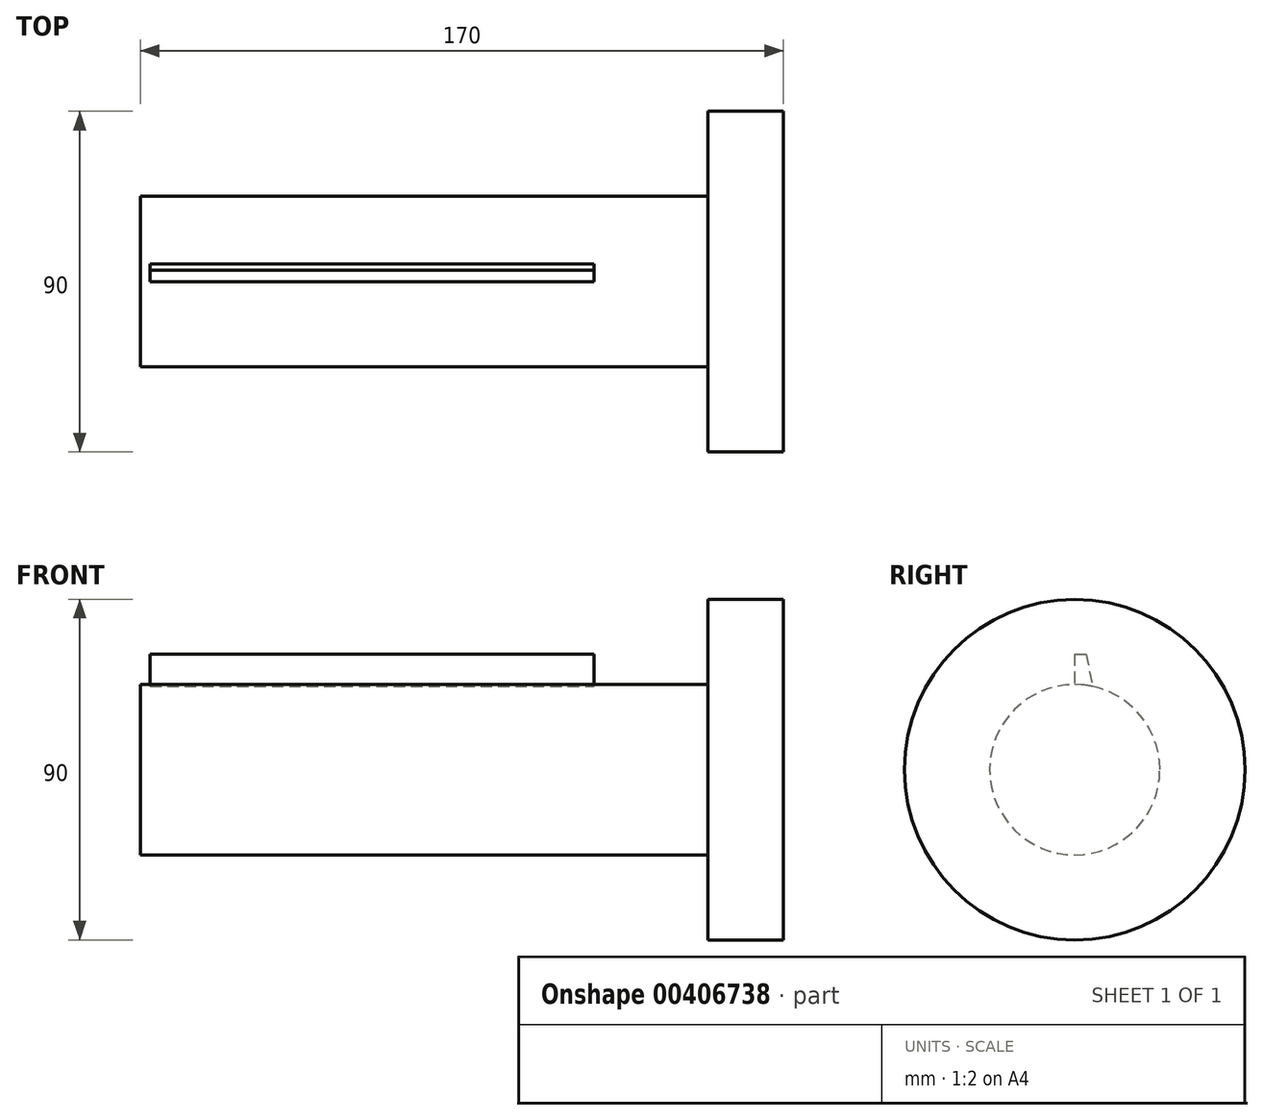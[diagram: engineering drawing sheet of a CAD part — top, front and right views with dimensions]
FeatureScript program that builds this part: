
annotation { "Feature Type Name" : "Feature", "Feature Type Description" : "" }
export const myFeature = defineFeature(function(context is Context, id is Id, definition is map)
    precondition{}
    {
        {
            var Q0;
            Q0=qCreatedBy(makeId("Front.planeOp"),FACE);
            var sketch = newSketch(context, id + "F0", { "sketchPlane" : qUnion([Q0])});
            skLineSegment(sketch, "E0", {"start": v(-150, 0) * mm, "end": v(20, 0) * mm});
            skLineSegment(sketch, "E1", {"start": v(20, 0) * mm, "end": v(20, 45) * mm});
            skLineSegment(sketch, "E2", {"start": v(20, 45) * mm, "end": v(0, 45) * mm});
            skLineSegment(sketch, "E3", {"start": v(0, 45) * mm, "end": v(0, 22.5) * mm});
            skLineSegment(sketch, "E4", {"start": v(0, 22.5) * mm, "end": v(-150, 22.5) * mm});
            skLineSegment(sketch, "E5", {"start": v(-150, 22.5) * mm, "end": v(-150, 0) * mm});
            skLineSegment(sketch, "E6", {"start": v(-127.35, 0) * mm, "end": v(126.66, 0) * mm, "construction": true});
            skSolve(sketch);
        }
        {
            var Q0;
            Q0 = qSketchRegion(id + "F0", true);
            var Q1;
            Q1=sQuery(id+"F0.wireOp",EDGE,"E6");
            revolve(context, id + "F1", {"entities" : qUnion([Q0]), "axis" : qUnion([Q1]), "revolveType" : RevolveType.FULL});
        }
        {
            var Q0;
            Q0=qCreatedBy(makeId("Right.planeOp"),FACE);
            cPlane(context, id + "F2", {"entities" : qUnion([Q0]), "cplaneType" : CPlaneType.OFFSET, "offset" : 30 * mm, "oppositeDirection" : true, "width" : 150 * mm, "height" : 150 * mm});
        }
        {
            var Q0;
            Q0=qCreatedBy(id+"F2.planeOp",FACE);
            var sketch = newSketch(context, id + "F3", { "sketchPlane" : qUnion([Q0])});
            skLineSegment(sketch, "E7", {"start": v(0, 127.28) * mm, "end": v(0, 0) * mm, "construction": true});
            skLineSegment(sketch, "E8", {"start": v(0, 0) * mm, "end": v(138.58, 0) * mm, "construction": true});
            skCircle(sketch, "E9", {"center": v(0, 0) * mm, "radius": 22.5 * mm, "construction": true});
            skLineSegment(sketch, "E10", {"start": v(0, 30.5) * mm, "end": v(3, 30.5) * mm});
            skLineSegment(sketch, "E11", {"start": v(3, 30.5) * mm, "end": v(4.67, 22) * mm});
            skLineSegment(sketch, "E12", {"start": v(0, 30.5) * mm, "end": v(0, 22.5) * mm});
            skLineSegment(sketch, "E13", {"start": v(4.67, 22) * mm, "end": v(0, 22.5) * mm});
            skSolve(sketch);
        }
        {
            var Q0;
            Q0 = qSketchRegion(id + "F3", true);
            extrude(context, id + "F4", {"entities" : qUnion([Q0]), "operationType" : NewBodyOperationType.ADD, "oppositeDirection" : true, "depth" : 117.4 * mm});
        }
    });
